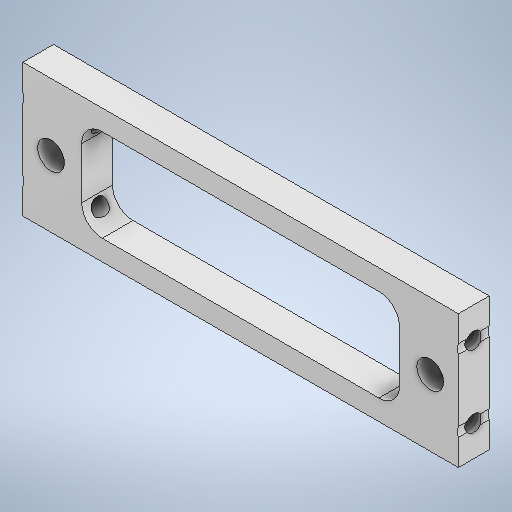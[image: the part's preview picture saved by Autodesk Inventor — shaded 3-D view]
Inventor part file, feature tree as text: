
AUTODESK INVENTOR PART (.ipt)
format: ipt  version: 2025.1 (Build 291241000, 241)  size: 335,872 bytes
history: native  units: mm
features: sketch x5, extrude x3, hole x2, other x1, fillet x1
ambient origin geometry x8: Origin, YZ Plane, XZ Plane, XY Plane, X Axis, Y Axis, Z Axis, Center Point
bodies: Body1 (feature_tree)
feature tree (12):
  other  "ソリッド1"
  extrude  "押し出し1"  Depth=2.6mm
  extrude  "押し出し2"  Depth=2.6mm
  fillet  "フィレット3"  Radius=37.0mm
  hole  "穴1"  [1 undecoded]
  hole  "穴2"  [1 undecoded]
  extrude  "押し出し8"  Depth=3.0mm TaperAngle=0.0deg
  sketch  "スケッチ1"
  sketch  "スケッチ2"
  sketch  "スケッチ9"
  sketch  "スケッチ10"
  sketch  "スケッチ11"
note: 2 required parameter values undecoded (feature->parameter linkage not recoverable at this tier; creation-order binding heuristic only, values carry confidence <= 0.55)
